# Revit family: Acoustical-EZPath-STI-EZ_Path_Series_33_Smoke_and_Acoustical_for_Ceilings
name_source: partatom
category: Generic Models
units: mm (PartAtom-declared; Revit-internal decimal feet)

## family parameters
Always vertical = Yes
Can host rebar = No
Cut with Voids When Loaded = No
Host = Ceiling
Maintain Annotation Orientation = No
Part Type = Normal
Room Calculation Point = No
Round Connector Dimension = Use Diameter
Shared = No

## types (1)
- Acoustical-EZPath-STI-EZ_Path_Series_33_Smoke_and_Acoustical_for_Ceilings
    Assembly Code = C3030210
    Default Elevation = 0' - 0"
    Description = EZ-Path Smoke & Acousitical Device Ceiling Kit
    EZ-Path Body = Acoustic-STI-EZPath-EZPath_Smoke_and_Acoustic_Device
    EZ-Path Face Plate = 0' - 4 7/8"
    EZ-Path Face Plate Corner = 0' - 0 1/2"
    Installation Instructions = http://files.systems.stifirestop.com
    Manufacturer = Specified Technologies, Inc
    Model = EZ-Path Series 33 Smoke & Acoustical Device
    Model No. (Complete Kit) = NEZ33CK2
    No. of Devices = 1
    Product Data Sheet = http://files.systems.stifirestop.com
    Product Page = https://www.stifirestop.com
    Region = North America
    Safety Data Sheet = https://files.stifirestop.com
    URL = https://www.stifirestop.com

## geometry (parser evidence)
native form markers: Blend x6, Sweep x2
no freeform markers — native parametric forms only
